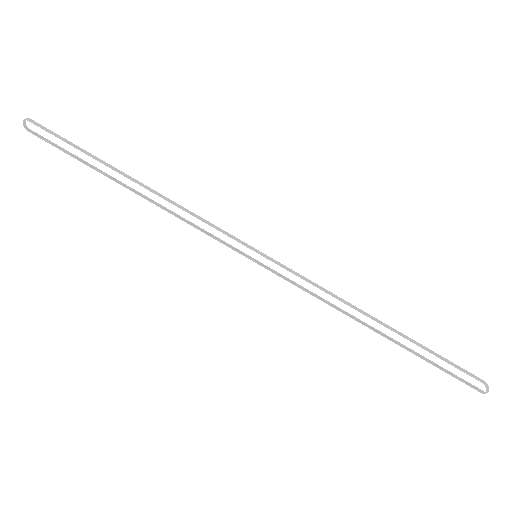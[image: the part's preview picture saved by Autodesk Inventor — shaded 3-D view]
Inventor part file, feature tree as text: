
AUTODESK INVENTOR PART (.ipt)
format: ipt  version: 2025.1 (Build 291241000, 241)  size: 11,118,592 bytes
history: native  units: mm
features: other x721, sketch x3, pattern_linear x2, extrude x2
ambient origin geometry x8: Origin, YZ Plane, XZ Plane, XY Plane, X Axis, Y Axis, Z Axis, Center Point
bodies: Body1 (feature_tree)
feature tree (728):
  other  "Bryła1"
  sketch  "Szkic1"
  other  "Punkt konstrukcyjny1"
  pattern_linear  "Szyk prostokątny1"  Spacing1=28.0mm  [1 undecoded]
  extrude  "Wyciągnięcie proste1"  Depth=1378.698mm
  pattern_linear  "Szyk prostokątny2"  Count1=720 Spacing1=10.0mm
  extrude  "Wyciągnięcie proste2"  Depth=1.0mm
  other  "Punkt konstrukcyjny2"
  other  "Punkt konstrukcyjny3"
  other  "Punkt konstrukcyjny4"
  other  "Punkt konstrukcyjny5"
  other  "Punkt konstrukcyjny6"
  other  "Punkt konstrukcyjny7"
  other  "Punkt konstrukcyjny8"
  other  "Punkt konstrukcyjny9"
  other  "Punkt konstrukcyjny10"
  other  "Punkt konstrukcyjny11"
  other  "Punkt konstrukcyjny12"
  other  "Punkt konstrukcyjny13"
  other  "Punkt konstrukcyjny14"
  other  "Punkt konstrukcyjny15"
  other  "Punkt konstrukcyjny16"
  other  "Punkt konstrukcyjny17"
  other  "Punkt konstrukcyjny18"
  other  "Punkt konstrukcyjny19"
  other  "Punkt konstrukcyjny20"
  other  "Punkt konstrukcyjny21"
  other  "Punkt konstrukcyjny22"
  other  "Punkt konstrukcyjny23"
  other  "Punkt konstrukcyjny24"
  other  "Punkt konstrukcyjny25"
  other  "Punkt konstrukcyjny26"
  other  "Punkt konstrukcyjny27"
  other  "Punkt konstrukcyjny28"
  other  "Punkt konstrukcyjny29"
  other  "Punkt konstrukcyjny30"
  other  "Punkt konstrukcyjny31"
  other  "Punkt konstrukcyjny32"
  other  "Punkt konstrukcyjny33"
  other  "Punkt konstrukcyjny34"
  other  "Punkt konstrukcyjny35"
  other  "Punkt konstrukcyjny36"
  other  "Punkt konstrukcyjny37"
  other  "Punkt konstrukcyjny38"
  other  "Punkt konstrukcyjny39"
  other  "Punkt konstrukcyjny40"
  other  "Punkt konstrukcyjny41"
  other  "Punkt konstrukcyjny42"
  other  "Punkt konstrukcyjny43"
  other  "Punkt konstrukcyjny44"
  other  "Punkt konstrukcyjny45"
  other  "Punkt konstrukcyjny46"
  other  "Punkt konstrukcyjny47"
  other  "Punkt konstrukcyjny48"
  other  "Punkt konstrukcyjny49"
  other  "Punkt konstrukcyjny50"
  other  "Punkt konstrukcyjny51"
  other  "Punkt konstrukcyjny52"
  other  "Punkt konstrukcyjny53"
  other  "Punkt konstrukcyjny54"
  other  "Punkt konstrukcyjny55"
  other  "Punkt konstrukcyjny56"
  other  "Punkt konstrukcyjny57"
  other  "Punkt konstrukcyjny58"
  other  "Punkt konstrukcyjny59"
  other  "Punkt konstrukcyjny60"
  other  "Punkt konstrukcyjny61"
  other  "Punkt konstrukcyjny62"
  other  "Punkt konstrukcyjny63"
  other  "Punkt konstrukcyjny64"
  other  "Punkt konstrukcyjny65"
  other  "Punkt konstrukcyjny66"
  other  "Punkt konstrukcyjny67"
  other  "Punkt konstrukcyjny68"
  other  "Punkt konstrukcyjny69"
  other  "Punkt konstrukcyjny70"
  other  "Punkt konstrukcyjny71"
  other  "Punkt konstrukcyjny72"
  other  "Punkt konstrukcyjny73"
  other  "Punkt konstrukcyjny74"
  other  "Punkt konstrukcyjny75"
  other  "Punkt konstrukcyjny76"
  other  "Punkt konstrukcyjny77"
  other  "Punkt konstrukcyjny78"
  other  "Punkt konstrukcyjny79"
  other  "Punkt konstrukcyjny80"
  other  "Punkt konstrukcyjny81"
  other  "Punkt konstrukcyjny82"
  other  "Punkt konstrukcyjny83"
  other  "Punkt konstrukcyjny84"
  other  "Punkt konstrukcyjny85"
  other  "Punkt konstrukcyjny86"
  other  "Punkt konstrukcyjny87"
  other  "Punkt konstrukcyjny88"
  other  "Punkt konstrukcyjny89"
  other  "Punkt konstrukcyjny90"
  other  "Punkt konstrukcyjny91"
  other  "Punkt konstrukcyjny92"
  other  "Punkt konstrukcyjny93"
  other  "Punkt konstrukcyjny94"
  other  "Punkt konstrukcyjny95"
  other  "Punkt konstrukcyjny96"
  other  "Punkt konstrukcyjny97"
  other  "Punkt konstrukcyjny98"
  other  "Punkt konstrukcyjny99"
  other  "Punkt konstrukcyjny100"
  other  "Punkt konstrukcyjny101"
  other  "Punkt konstrukcyjny102"
  other  "Punkt konstrukcyjny103"
  other  "Punkt konstrukcyjny104"
  other  "Punkt konstrukcyjny105"
  other  "Punkt konstrukcyjny106"
  other  "Punkt konstrukcyjny107"
  other  "Punkt konstrukcyjny108"
  other  "Punkt konstrukcyjny109"
  other  "Punkt konstrukcyjny110"
  other  "Punkt konstrukcyjny111"
  other  "Punkt konstrukcyjny112"
  other  "Punkt konstrukcyjny113"
  other  "Punkt konstrukcyjny114"
  other  "Punkt konstrukcyjny115"
  other  "Punkt konstrukcyjny116"
  other  "Punkt konstrukcyjny117"
  other  "Punkt konstrukcyjny118"
  other  "Punkt konstrukcyjny119"
  other  "Punkt konstrukcyjny120"
  other  "Punkt konstrukcyjny121"
  other  "Punkt konstrukcyjny122"
  other  "Punkt konstrukcyjny123"
  other  "Punkt konstrukcyjny124"
  other  "Punkt konstrukcyjny125"
  other  "Punkt konstrukcyjny126"
  other  "Punkt konstrukcyjny127"
  other  "Punkt konstrukcyjny128"
  other  "Punkt konstrukcyjny129"
  other  "Punkt konstrukcyjny130"
  other  "Punkt konstrukcyjny131"
  other  "Punkt konstrukcyjny132"
  other  "Punkt konstrukcyjny133"
  other  "Punkt konstrukcyjny134"
  other  "Punkt konstrukcyjny135"
  other  "Punkt konstrukcyjny136"
  other  "Punkt konstrukcyjny137"
  other  "Punkt konstrukcyjny138"
  other  "Punkt konstrukcyjny139"
  other  "Punkt konstrukcyjny140"
  other  "Punkt konstrukcyjny141"
  other  "Punkt konstrukcyjny142"
  other  "Punkt konstrukcyjny143"
  other  "Punkt konstrukcyjny144"
  other  "Punkt konstrukcyjny145"
  other  "Punkt konstrukcyjny146"
  other  "Punkt konstrukcyjny147"
  other  "Punkt konstrukcyjny148"
  other  "Punkt konstrukcyjny149"
  other  "Punkt konstrukcyjny150"
  other  "Punkt konstrukcyjny151"
  other  "Punkt konstrukcyjny152"
  other  "Punkt konstrukcyjny153"
  other  "Punkt konstrukcyjny154"
  other  "Punkt konstrukcyjny155"
  other  "Punkt konstrukcyjny156"
  other  "Punkt konstrukcyjny157"
  other  "Punkt konstrukcyjny158"
  other  "Punkt konstrukcyjny159"
  other  "Punkt konstrukcyjny160"
  other  "Punkt konstrukcyjny161"
  other  "Punkt konstrukcyjny162"
  other  "Punkt konstrukcyjny163"
  other  "Punkt konstrukcyjny164"
  other  "Punkt konstrukcyjny165"
  other  "Punkt konstrukcyjny166"
  other  "Punkt konstrukcyjny167"
  other  "Punkt konstrukcyjny168"
  other  "Punkt konstrukcyjny169"
  other  "Punkt konstrukcyjny170"
  other  "Punkt konstrukcyjny171"
  other  "Punkt konstrukcyjny172"
  other  "Punkt konstrukcyjny173"
  other  "Punkt konstrukcyjny174"
  other  "Punkt konstrukcyjny175"
  other  "Punkt konstrukcyjny176"
  other  "Punkt konstrukcyjny177"
  other  "Punkt konstrukcyjny178"
  other  "Punkt konstrukcyjny179"
  other  "Punkt konstrukcyjny180"
  other  "Punkt konstrukcyjny181"
  other  "Punkt konstrukcyjny182"
  other  "Punkt konstrukcyjny183"
  other  "Punkt konstrukcyjny184"
  other  "Punkt konstrukcyjny185"
  other  "Punkt konstrukcyjny186"
  other  "Punkt konstrukcyjny187"
  other  "Punkt konstrukcyjny188"
  other  "Punkt konstrukcyjny189"
  other  "Punkt konstrukcyjny190"
  other  "Punkt konstrukcyjny191"
  other  "Punkt konstrukcyjny192"
  other  "Punkt konstrukcyjny193"
  other  "Punkt konstrukcyjny194"
  other  "Punkt konstrukcyjny195"
  other  "Punkt konstrukcyjny196"
  other  "Punkt konstrukcyjny197"
  other  "Punkt konstrukcyjny198"
  other  "Punkt konstrukcyjny199"
  other  "Punkt konstrukcyjny200"
  other  "Punkt konstrukcyjny201"
  other  "Punkt konstrukcyjny202"
  other  "Punkt konstrukcyjny203"
  other  "Punkt konstrukcyjny204"
  other  "Punkt konstrukcyjny205"
  other  "Punkt konstrukcyjny206"
  other  "Punkt konstrukcyjny207"
  other  "Punkt konstrukcyjny208"
  other  "Punkt konstrukcyjny209"
  other  "Punkt konstrukcyjny210"
  other  "Punkt konstrukcyjny211"
  other  "Punkt konstrukcyjny212"
  other  "Punkt konstrukcyjny213"
  other  "Punkt konstrukcyjny214"
  other  "Punkt konstrukcyjny215"
  other  "Punkt konstrukcyjny216"
  other  "Punkt konstrukcyjny217"
  other  "Punkt konstrukcyjny218"
  other  "Punkt konstrukcyjny219"
  other  "Punkt konstrukcyjny220"
  other  "Punkt konstrukcyjny221"
  other  "Punkt konstrukcyjny222"
  other  "Punkt konstrukcyjny223"
  other  "Punkt konstrukcyjny224"
  other  "Punkt konstrukcyjny225"
  other  "Punkt konstrukcyjny226"
  other  "Punkt konstrukcyjny227"
  other  "Punkt konstrukcyjny228"
  other  "Punkt konstrukcyjny229"
  other  "Punkt konstrukcyjny230"
  other  "Punkt konstrukcyjny231"
  other  "Punkt konstrukcyjny232"
  other  "Punkt konstrukcyjny233"
  other  "Punkt konstrukcyjny234"
  other  "Punkt konstrukcyjny235"
  other  "Punkt konstrukcyjny236"
  other  "Punkt konstrukcyjny237"
  other  "Punkt konstrukcyjny238"
  other  "Punkt konstrukcyjny239"
  other  "Punkt konstrukcyjny240"
  other  "Punkt konstrukcyjny361"
  other  "Punkt konstrukcyjny362"
  other  "Punkt konstrukcyjny363"
  other  "Punkt konstrukcyjny364"
  other  "Punkt konstrukcyjny365"
  other  "Punkt konstrukcyjny366"
  other  "Punkt konstrukcyjny367"
  other  "Punkt konstrukcyjny368"
  other  "Punkt konstrukcyjny369"
  other  "Punkt konstrukcyjny370"
  other  "Punkt konstrukcyjny371"
  other  "Punkt konstrukcyjny372"
  other  "Punkt konstrukcyjny373"
  other  "Punkt konstrukcyjny374"
  other  "Punkt konstrukcyjny375"
  other  "Punkt konstrukcyjny376"
  other  "Punkt konstrukcyjny377"
  other  "Punkt konstrukcyjny378"
  other  "Punkt konstrukcyjny379"
  other  "Punkt konstrukcyjny380"
  other  "Punkt konstrukcyjny381"
  other  "Punkt konstrukcyjny382"
  other  "Punkt konstrukcyjny383"
  other  "Punkt konstrukcyjny384"
  other  "Punkt konstrukcyjny385"
  other  "Punkt konstrukcyjny386"
  other  "Punkt konstrukcyjny387"
  other  "Punkt konstrukcyjny388"
  other  "Punkt konstrukcyjny389"
  other  "Punkt konstrukcyjny390"
  other  "Punkt konstrukcyjny391"
  other  "Punkt konstrukcyjny392"
  other  "Punkt konstrukcyjny393"
  other  "Punkt konstrukcyjny394"
  other  "Punkt konstrukcyjny395"
  other  "Punkt konstrukcyjny396"
  other  "Punkt konstrukcyjny397"
  other  "Punkt konstrukcyjny398"
  other  "Punkt konstrukcyjny399"
  other  "Punkt konstrukcyjny400"
  other  "Punkt konstrukcyjny401"
  other  "Punkt konstrukcyjny402"
  other  "Punkt konstrukcyjny403"
  other  "Punkt konstrukcyjny404"
  other  "Punkt konstrukcyjny405"
  other  "Punkt konstrukcyjny406"
  other  "Punkt konstrukcyjny407"
  other  "Punkt konstrukcyjny408"
  other  "Punkt konstrukcyjny409"
  other  "Punkt konstrukcyjny410"
  other  "Punkt konstrukcyjny411"
  other  "Punkt konstrukcyjny412"
  other  "Punkt konstrukcyjny413"
  other  "Punkt konstrukcyjny414"
  other  "Punkt konstrukcyjny415"
  other  "Punkt konstrukcyjny416"
  other  "Punkt konstrukcyjny417"
  other  "Punkt konstrukcyjny418"
  other  "Punkt konstrukcyjny419"
  other  "Punkt konstrukcyjny420"
  other  "Punkt konstrukcyjny421"
  other  "Punkt konstrukcyjny422"
  other  "Punkt konstrukcyjny423"
  other  "Punkt konstrukcyjny424"
  other  "Punkt konstrukcyjny425"
  other  "Punkt konstrukcyjny426"
  other  "Punkt konstrukcyjny427"
  other  "Punkt konstrukcyjny428"
  other  "Punkt konstrukcyjny429"
  other  "Punkt konstrukcyjny430"
  other  "Punkt konstrukcyjny431"
  other  "Punkt konstrukcyjny432"
  other  "Punkt konstrukcyjny433"
  other  "Punkt konstrukcyjny434"
  other  "Punkt konstrukcyjny435"
  other  "Punkt konstrukcyjny436"
  other  "Punkt konstrukcyjny437"
  other  "Punkt konstrukcyjny438"
  other  "Punkt konstrukcyjny439"
  other  "Punkt konstrukcyjny440"
  other  "Punkt konstrukcyjny441"
  other  "Punkt konstrukcyjny442"
  other  "Punkt konstrukcyjny443"
  other  "Punkt konstrukcyjny444"
  other  "Punkt konstrukcyjny445"
  other  "Punkt konstrukcyjny446"
  other  "Punkt konstrukcyjny447"
  other  "Punkt konstrukcyjny448"
  other  "Punkt konstrukcyjny449"
  other  "Punkt konstrukcyjny450"
  other  "Punkt konstrukcyjny451"
  other  "Punkt konstrukcyjny452"
  other  "Punkt konstrukcyjny453"
  other  "Punkt konstrukcyjny454"
  other  "Punkt konstrukcyjny455"
  other  "Punkt konstrukcyjny456"
  other  "Punkt konstrukcyjny457"
  other  "Punkt konstrukcyjny458"
  other  "Punkt konstrukcyjny459"
  other  "Punkt konstrukcyjny460"
  other  "Punkt konstrukcyjny461"
  other  "Punkt konstrukcyjny462"
  other  "Punkt konstrukcyjny463"
  other  "Punkt konstrukcyjny464"
  other  "Punkt konstrukcyjny465"
  other  "Punkt konstrukcyjny466"
  other  "Punkt konstrukcyjny467"
  other  "Punkt konstrukcyjny468"
  other  "Punkt konstrukcyjny469"
  other  "Punkt konstrukcyjny470"
  other  "Punkt konstrukcyjny471"
  other  "Punkt konstrukcyjny472"
  other  "Punkt konstrukcyjny473"
  other  "Punkt konstrukcyjny474"
  other  "Punkt konstrukcyjny475"
  other  "Punkt konstrukcyjny476"
  other  "Punkt konstrukcyjny477"
  other  "Punkt konstrukcyjny478"
  other  "Punkt konstrukcyjny479"
  other  "Punkt konstrukcyjny480"
  other  "Punkt konstrukcyjny481"
  other  "Punkt konstrukcyjny482"
  other  "Punkt konstrukcyjny483"
  other  "Punkt konstrukcyjny484"
  other  "Punkt konstrukcyjny485"
  other  "Punkt konstrukcyjny486"
  other  "Punkt konstrukcyjny487"
  other  "Punkt konstrukcyjny488"
  other  "Punkt konstrukcyjny489"
  other  "Punkt konstrukcyjny490"
  other  "Punkt konstrukcyjny491"
  other  "Punkt konstrukcyjny492"
  other  "Punkt konstrukcyjny493"
  other  "Punkt konstrukcyjny494"
  other  "Punkt konstrukcyjny495"
  other  "Punkt konstrukcyjny496"
  other  "Punkt konstrukcyjny497"
  other  "Punkt konstrukcyjny498"
  other  "Punkt konstrukcyjny499"
  other  "Punkt konstrukcyjny500"
  other  "Punkt konstrukcyjny501"
  other  "Punkt konstrukcyjny502"
  other  "Punkt konstrukcyjny503"
  other  "Punkt konstrukcyjny504"
  other  "Punkt konstrukcyjny505"
  other  "Punkt konstrukcyjny506"
  other  "Punkt konstrukcyjny507"
  other  "Punkt konstrukcyjny508"
  other  "Punkt konstrukcyjny509"
  other  "Punkt konstrukcyjny510"
  other  "Punkt konstrukcyjny511"
  other  "Punkt konstrukcyjny512"
  other  "Punkt konstrukcyjny513"
  other  "Punkt konstrukcyjny514"
  other  "Punkt konstrukcyjny515"
  other  "Punkt konstrukcyjny516"
  other  "Punkt konstrukcyjny517"
  other  "Punkt konstrukcyjny518"
  other  "Punkt konstrukcyjny519"
  other  "Punkt konstrukcyjny520"
  other  "Punkt konstrukcyjny521"
  other  "Punkt konstrukcyjny522"
  other  "Punkt konstrukcyjny523"
  other  "Punkt konstrukcyjny524"
  other  "Punkt konstrukcyjny525"
  other  "Punkt konstrukcyjny526"
  other  "Punkt konstrukcyjny527"
  other  "Punkt konstrukcyjny528"
  other  "Punkt konstrukcyjny529"
  other  "Punkt konstrukcyjny530"
  other  "Punkt konstrukcyjny531"
  other  "Punkt konstrukcyjny532"
  other  "Punkt konstrukcyjny533"
  other  "Punkt konstrukcyjny534"
  other  "Punkt konstrukcyjny535"
  other  "Punkt konstrukcyjny536"
  other  "Punkt konstrukcyjny537"
  other  "Punkt konstrukcyjny538"
  other  "Punkt konstrukcyjny539"
  other  "Punkt konstrukcyjny540"
  other  "Punkt konstrukcyjny541"
  other  "Punkt konstrukcyjny542"
  other  "Punkt konstrukcyjny543"
  other  "Punkt konstrukcyjny544"
  other  "Punkt konstrukcyjny545"
  other  "Punkt konstrukcyjny546"
  other  "Punkt konstrukcyjny547"
  other  "Punkt konstrukcyjny548"
  other  "Punkt konstrukcyjny549"
  other  "Punkt konstrukcyjny550"
  other  "Punkt konstrukcyjny551"
  other  "Punkt konstrukcyjny552"
  other  "Punkt konstrukcyjny553"
  other  "Punkt konstrukcyjny554"
  other  "Punkt konstrukcyjny555"
  other  "Punkt konstrukcyjny556"
  other  "Punkt konstrukcyjny557"
  other  "Punkt konstrukcyjny558"
  other  "Punkt konstrukcyjny559"
  other  "Punkt konstrukcyjny560"
  other  "Punkt konstrukcyjny561"
  other  "Punkt konstrukcyjny562"
  other  "Punkt konstrukcyjny563"
  other  "Punkt konstrukcyjny564"
  other  "Punkt konstrukcyjny565"
  other  "Punkt konstrukcyjny566"
  other  "Punkt konstrukcyjny567"
  other  "Punkt konstrukcyjny568"
  other  "Punkt konstrukcyjny569"
  other  "Punkt konstrukcyjny570"
  other  "Punkt konstrukcyjny571"
  other  "Punkt konstrukcyjny572"
  other  "Punkt konstrukcyjny573"
  other  "Punkt konstrukcyjny574"
  other  "Punkt konstrukcyjny575"
  other  "Punkt konstrukcyjny576"
  other  "Punkt konstrukcyjny577"
  other  "Punkt konstrukcyjny578"
  other  "Punkt konstrukcyjny579"
  other  "Punkt konstrukcyjny580"
  other  "Punkt konstrukcyjny581"
  other  "Punkt konstrukcyjny582"
  other  "Punkt konstrukcyjny583"
  other  "Punkt konstrukcyjny584"
  other  "Punkt konstrukcyjny585"
  other  "Punkt konstrukcyjny586"
  other  "Punkt konstrukcyjny587"
  other  "Punkt konstrukcyjny588"
  other  "Punkt konstrukcyjny589"
  other  "Punkt konstrukcyjny590"
  other  "Punkt konstrukcyjny591"
  other  "Punkt konstrukcyjny592"
  other  "Punkt konstrukcyjny593"
  other  "Punkt konstrukcyjny594"
  other  "Punkt konstrukcyjny595"
  other  "Punkt konstrukcyjny596"
  other  "Punkt konstrukcyjny597"
  other  "Punkt konstrukcyjny598"
  other  "Punkt konstrukcyjny599"
  other  "Punkt konstrukcyjny600"
  other  "Punkt konstrukcyjny601"
  other  "Punkt konstrukcyjny602"
  other  "Punkt konstrukcyjny603"
  other  "Punkt konstrukcyjny604"
  other  "Punkt konstrukcyjny605"
  other  "Punkt konstrukcyjny606"
  other  "Punkt konstrukcyjny607"
  other  "Punkt konstrukcyjny608"
  other  "Punkt konstrukcyjny609"
  other  "Punkt konstrukcyjny610"
  other  "Punkt konstrukcyjny611"
  other  "Punkt konstrukcyjny612"
  other  "Punkt konstrukcyjny613"
  other  "Punkt konstrukcyjny614"
  other  "Punkt konstrukcyjny615"
  other  "Punkt konstrukcyjny616"
  other  "Punkt konstrukcyjny617"
  other  "Punkt konstrukcyjny618"
  other  "Punkt konstrukcyjny619"
  other  "Punkt konstrukcyjny620"
  other  "Punkt konstrukcyjny621"
  other  "Punkt konstrukcyjny622"
  other  "Punkt konstrukcyjny623"
  other  "Punkt konstrukcyjny624"
  other  "Punkt konstrukcyjny625"
  other  "Punkt konstrukcyjny626"
  other  "Punkt konstrukcyjny627"
  other  "Punkt konstrukcyjny628"
  other  "Punkt konstrukcyjny629"
  other  "Punkt konstrukcyjny630"
  other  "Punkt konstrukcyjny631"
  other  "Punkt konstrukcyjny632"
  other  "Punkt konstrukcyjny633"
  other  "Punkt konstrukcyjny634"
  other  "Punkt konstrukcyjny635"
  other  "Punkt konstrukcyjny636"
  other  "Punkt konstrukcyjny637"
  other  "Punkt konstrukcyjny638"
  other  "Punkt konstrukcyjny639"
  other  "Punkt konstrukcyjny640"
  other  "Punkt konstrukcyjny641"
  other  "Punkt konstrukcyjny642"
  other  "Punkt konstrukcyjny643"
  other  "Punkt konstrukcyjny644"
  other  "Punkt konstrukcyjny645"
  other  "Punkt konstrukcyjny646"
  other  "Punkt konstrukcyjny647"
  other  "Punkt konstrukcyjny648"
  other  "Punkt konstrukcyjny649"
  other  "Punkt konstrukcyjny650"
  other  "Punkt konstrukcyjny651"
  other  "Punkt konstrukcyjny652"
  other  "Punkt konstrukcyjny653"
  other  "Punkt konstrukcyjny654"
  other  "Punkt konstrukcyjny655"
  other  "Punkt konstrukcyjny656"
  other  "Punkt konstrukcyjny657"
  other  "Punkt konstrukcyjny658"
  other  "Punkt konstrukcyjny659"
  other  "Punkt konstrukcyjny660"
  other  "Punkt konstrukcyjny661"
  other  "Punkt konstrukcyjny662"
  other  "Punkt konstrukcyjny663"
  other  "Punkt konstrukcyjny664"
  other  "Punkt konstrukcyjny665"
  other  "Punkt konstrukcyjny666"
  other  "Punkt konstrukcyjny667"
  other  "Punkt konstrukcyjny668"
  other  "Punkt konstrukcyjny669"
  other  "Punkt konstrukcyjny670"
  other  "Punkt konstrukcyjny671"
  other  "Punkt konstrukcyjny672"
  other  "Punkt konstrukcyjny673"
  other  "Punkt konstrukcyjny674"
  other  "Punkt konstrukcyjny675"
  other  "Punkt konstrukcyjny676"
  other  "Punkt konstrukcyjny677"
  other  "Punkt konstrukcyjny678"
  other  "Punkt konstrukcyjny679"
  other  "Punkt konstrukcyjny680"
  other  "Punkt konstrukcyjny681"
  other  "Punkt konstrukcyjny682"
  other  "Punkt konstrukcyjny683"
  other  "Punkt konstrukcyjny684"
  other  "Punkt konstrukcyjny685"
  other  "Punkt konstrukcyjny686"
  other  "Punkt konstrukcyjny687"
  other  "Punkt konstrukcyjny688"
  other  "Punkt konstrukcyjny689"
  other  "Punkt konstrukcyjny690"
  other  "Punkt konstrukcyjny691"
  other  "Punkt konstrukcyjny692"
  other  "Punkt konstrukcyjny693"
  other  "Punkt konstrukcyjny694"
  other  "Punkt konstrukcyjny695"
  other  "Punkt konstrukcyjny696"
  other  "Punkt konstrukcyjny697"
  other  "Punkt konstrukcyjny698"
  other  "Punkt konstrukcyjny699"
  other  "Punkt konstrukcyjny700"
  other  "Punkt konstrukcyjny701"
  other  "Punkt konstrukcyjny702"
  other  "Punkt konstrukcyjny703"
  other  "Punkt konstrukcyjny704"
  other  "Punkt konstrukcyjny705"
  other  "Punkt konstrukcyjny706"
  other  "Punkt konstrukcyjny707"
  other  "Punkt konstrukcyjny708"
  other  "Punkt konstrukcyjny709"
  other  "Punkt konstrukcyjny710"
  other  "Punkt konstrukcyjny711"
  other  "Punkt konstrukcyjny712"
  other  "Punkt konstrukcyjny713"
  other  "Punkt konstrukcyjny714"
  other  "Punkt konstrukcyjny715"
  other  "Punkt konstrukcyjny716"
  other  "Punkt konstrukcyjny717"
  other  "Punkt konstrukcyjny718"
  other  "Punkt konstrukcyjny719"
  other  "Punkt konstrukcyjny720"
  other  "Punkt konstrukcyjny721"
  other  "Punkt konstrukcyjny722"
  other  "Punkt konstrukcyjny723"
  other  "Punkt konstrukcyjny724"
  other  "Punkt konstrukcyjny725"
  other  "Punkt konstrukcyjny726"
  other  "Punkt konstrukcyjny727"
  other  "Punkt konstrukcyjny728"
  other  "Punkt konstrukcyjny729"
  other  "Punkt konstrukcyjny730"
  other  "Punkt konstrukcyjny731"
  other  "Punkt konstrukcyjny732"
  other  "Punkt konstrukcyjny733"
  other  "Punkt konstrukcyjny734"
  other  "Punkt konstrukcyjny735"
  other  "Punkt konstrukcyjny736"
  other  "Punkt konstrukcyjny737"
  other  "Punkt konstrukcyjny738"
  other  "Punkt konstrukcyjny739"
  other  "Punkt konstrukcyjny740"
  other  "Punkt konstrukcyjny741"
  other  "Punkt konstrukcyjny742"
  other  "Punkt konstrukcyjny743"
  other  "Punkt konstrukcyjny744"
  other  "Punkt konstrukcyjny745"
  other  "Punkt konstrukcyjny746"
  other  "Punkt konstrukcyjny747"
  other  "Punkt konstrukcyjny748"
  other  "Punkt konstrukcyjny749"
  other  "Punkt konstrukcyjny750"
  other  "Punkt konstrukcyjny751"
  other  "Punkt konstrukcyjny752"
  other  "Punkt konstrukcyjny753"
  other  "Punkt konstrukcyjny754"
  other  "Punkt konstrukcyjny755"
  other  "Punkt konstrukcyjny756"
  other  "Punkt konstrukcyjny757"
  other  "Punkt konstrukcyjny758"
  other  "Punkt konstrukcyjny759"
  other  "Punkt konstrukcyjny760"
  other  "Punkt konstrukcyjny761"
  other  "Punkt konstrukcyjny762"
  other  "Punkt konstrukcyjny763"
  other  "Punkt konstrukcyjny764"
  other  "Punkt konstrukcyjny765"
  other  "Punkt konstrukcyjny766"
  other  "Punkt konstrukcyjny767"
  other  "Punkt konstrukcyjny768"
  other  "Punkt konstrukcyjny769"
  other  "Punkt konstrukcyjny770"
  other  "Punkt konstrukcyjny771"
  other  "Punkt konstrukcyjny772"
  other  "Punkt konstrukcyjny773"
  other  "Punkt konstrukcyjny774"
  other  "Punkt konstrukcyjny775"
  other  "Punkt konstrukcyjny776"
  other  "Punkt konstrukcyjny777"
  other  "Punkt konstrukcyjny778"
  other  "Punkt konstrukcyjny779"
  other  "Punkt konstrukcyjny780"
  other  "Punkt konstrukcyjny781"
  other  "Punkt konstrukcyjny782"
  other  "Punkt konstrukcyjny783"
  other  "Punkt konstrukcyjny784"
  other  "Punkt konstrukcyjny785"
  other  "Punkt konstrukcyjny786"
  other  "Punkt konstrukcyjny787"
  other  "Punkt konstrukcyjny788"
  other  "Punkt konstrukcyjny789"
  other  "Punkt konstrukcyjny790"
  other  "Punkt konstrukcyjny791"
  other  "Punkt konstrukcyjny792"
  other  "Punkt konstrukcyjny793"
  other  "Punkt konstrukcyjny794"
  other  "Punkt konstrukcyjny795"
  other  "Punkt konstrukcyjny796"
  other  "Punkt konstrukcyjny797"
  other  "Punkt konstrukcyjny798"
  other  "Punkt konstrukcyjny799"
  other  "Punkt konstrukcyjny800"
  other  "Punkt konstrukcyjny801"
  other  "Punkt konstrukcyjny802"
  other  "Punkt konstrukcyjny803"
  other  "Punkt konstrukcyjny804"
  other  "Punkt konstrukcyjny805"
  other  "Punkt konstrukcyjny806"
  other  "Punkt konstrukcyjny807"
  other  "Punkt konstrukcyjny808"
  other  "Punkt konstrukcyjny809"
  other  "Punkt konstrukcyjny810"
  other  "Punkt konstrukcyjny811"
  other  "Punkt konstrukcyjny812"
  other  "Punkt konstrukcyjny813"
  other  "Punkt konstrukcyjny814"
  other  "Punkt konstrukcyjny815"
  other  "Punkt konstrukcyjny816"
  other  "Punkt konstrukcyjny817"
  other  "Punkt konstrukcyjny818"
  other  "Punkt konstrukcyjny819"
  other  "Punkt konstrukcyjny820"
  other  "Punkt konstrukcyjny821"
  other  "Punkt konstrukcyjny822"
  other  "Punkt konstrukcyjny823"
  other  "Punkt konstrukcyjny824"
  other  "Punkt konstrukcyjny825"
  other  "Punkt konstrukcyjny826"
  other  "Punkt konstrukcyjny827"
  other  "Punkt konstrukcyjny828"
  other  "Punkt konstrukcyjny829"
  other  "Punkt konstrukcyjny830"
  other  "Punkt konstrukcyjny831"
  other  "Punkt konstrukcyjny832"
  other  "Punkt konstrukcyjny833"
  other  "Punkt konstrukcyjny834"
  other  "Punkt konstrukcyjny835"
  other  "Punkt konstrukcyjny836"
  other  "Punkt konstrukcyjny837"
  other  "Punkt konstrukcyjny838"
  other  "Punkt konstrukcyjny839"
  other  "Punkt konstrukcyjny840"
  sketch  "Szkic4"
  sketch  "Szkic5"
note: 1 required parameter value undecoded (feature->parameter linkage not recoverable at this tier; creation-order binding heuristic only, values carry confidence <= 0.55)
